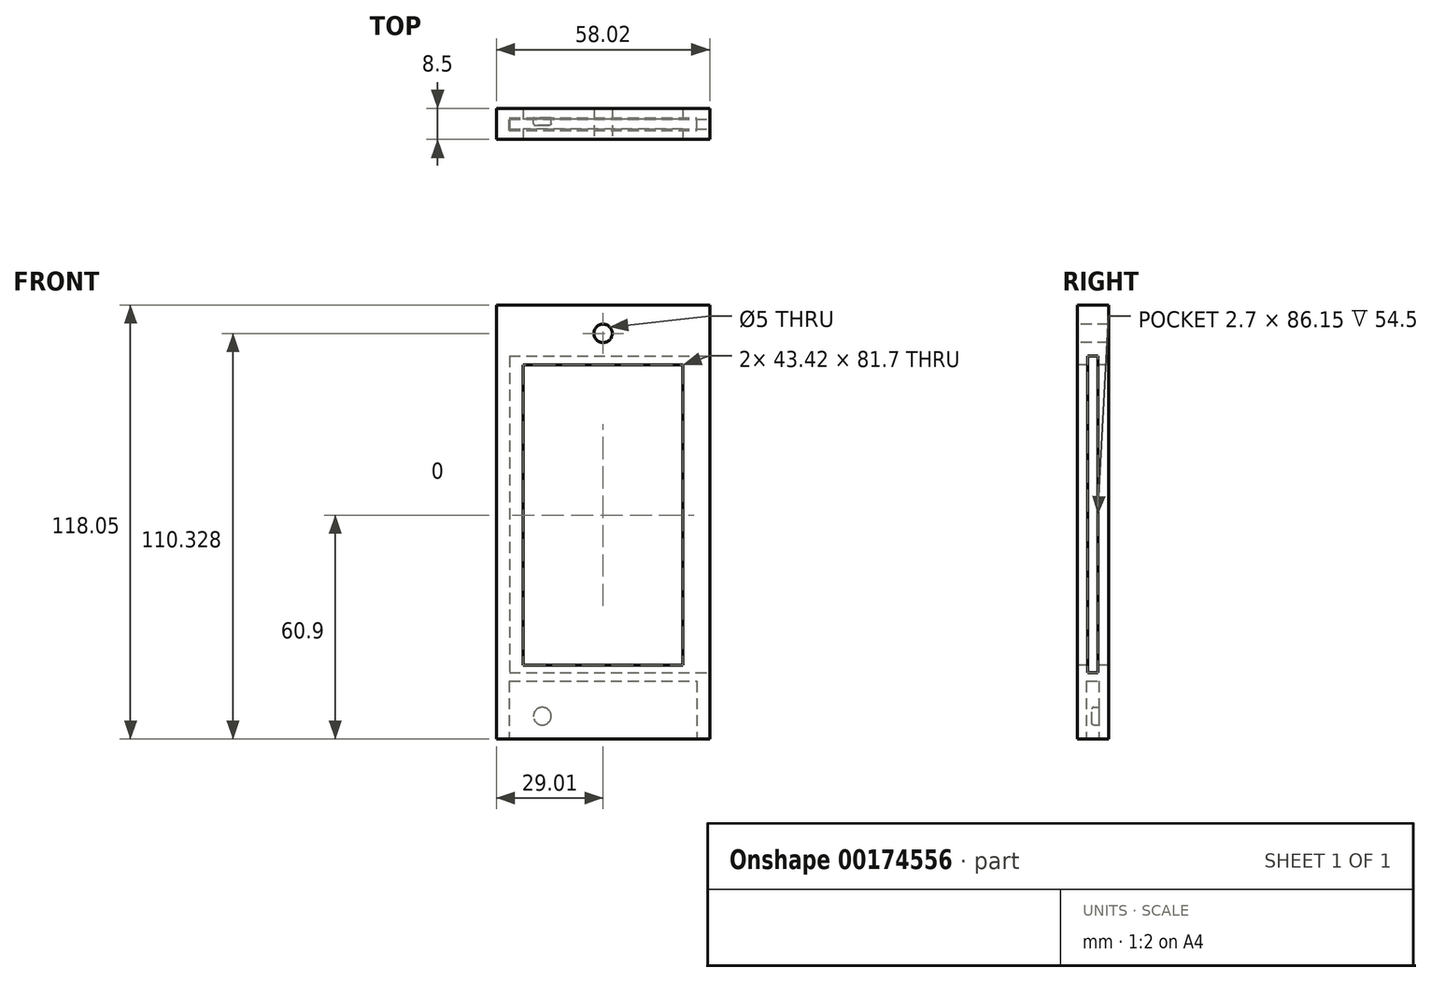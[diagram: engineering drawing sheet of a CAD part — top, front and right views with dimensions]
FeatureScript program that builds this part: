
annotation { "Feature Type Name" : "Feature", "Feature Type Description" : "" }
export const myFeature = defineFeature(function(context is Context, id is Id, definition is map)
    precondition{}
    {
        {
            var Q0;
            Q0=qCreatedBy(makeId("Front.planeOp"),FACE);
            var sketch = newSketch(context, id + "F0", { "sketchPlane" : qUnion([Q0])});
            skLineSegment(sketch, "E0.bottom", {"start": v(-29, 48.15) * mm, "end": v(29.01, 48.15) * mm});
            skLineSegment(sketch, "E0.top", {"start": v(-29.01, -48.15) * mm, "end": v(29.01, -48.15) * mm});
            skLineSegment(sketch, "E0.left", {"start": v(-29, 48.15) * mm, "end": v(-29.01, -48.15) * mm});
            skLineSegment(sketch, "E0.right", {"start": v(29.01, 48.15) * mm, "end": v(29, -48.15) * mm});
            skPoint(sketch, "E0.middle", {"position": v(0, 0) * mm});
            skSolve(sketch);
        }
        {
            var Q0;
            Q0=makeQuery(id+"F0.imprint","IMPRINT",FACE,{"disambiguationData":[TD([[makeQuery(id+"F0.imprint","IMPRINT",EDGE,{"derivedFrom":sQuery(id+"F0.wireOp",EDGE,"E0.bottom")}),-1.0]])]});
            extrude(context, id + "F1", {"entities" : qUnion([Q0]), "depth" : 5.5 * mm});
        }
        {
            var Q0;
            Q0=makeQuery(id+"F1.opExtrude","CAP_FACE",FACE,{"disambiguationData":[OSD([sQuery(id+"F0.wireOp",EDGE,"E0.bottom"),sQuery(id+"F0.wireOp",EDGE,"E0.top"),sQuery(id+"F0.wireOp",EDGE,"E0.left"),sQuery(id+"F0.wireOp",EDGE,"E0.right")])],"isStart":false});
            var sketch = newSketch(context, id + "F2", { "sketchPlane" : qUnion([Q0])});
            skLineSegment(sketch, "E1.bottom", {"start": v(-21.7, 40.85) * mm, "end": v(21.71, 40.85) * mm});
            skLineSegment(sketch, "E1.top", {"start": v(-21.71, -40.85) * mm, "end": v(21.7, -40.85) * mm});
            skLineSegment(sketch, "E1.left", {"start": v(-21.7, 40.85) * mm, "end": v(-21.71, -40.85) * mm});
            skLineSegment(sketch, "E1.right", {"start": v(21.71, 40.85) * mm, "end": v(21.7, -40.85) * mm});
            skPoint(sketch, "E1.middle", {"position": v(0, 0) * mm});
            skSolve(sketch);
        }
        {
            var Q0;
            Q0 = qSketchRegion(id + "F2", true);
            extrude(context, id + "F3", {"entities" : qUnion([Q0]), "operationType" : NewBodyOperationType.REMOVE, "endBound" : BoundingType.THROUGH_ALL, "oppositeDirection" : true, "depth" : 25 * mm});
        }
        {
            var Q0;
            Q0=makeQuery(id+"F1.opExtrude","SWEPT_FACE",FACE,{"disambiguationData":[OSD([sQuery(id+"F0.wireOp",EDGE,"E0.right")])]});
            var sketch = newSketch(context, id + "F4", { "sketchPlane" : qUnion([Q0])});
            skPoint(sketch, "E2", {"position": v(-2.67, 0) * mm});
            skLineSegment(sketch, "E3.bottom", {"start": v(-1.47, 42.88) * mm, "end": v(-3.87, 42.88) * mm});
            skLineSegment(sketch, "E3.top", {"start": v(-1.47, -42.88) * mm, "end": v(-3.87, -42.88) * mm});
            skLineSegment(sketch, "E3.left", {"start": v(-1.47, 42.88) * mm, "end": v(-1.47, -42.88) * mm});
            skLineSegment(sketch, "E3.right", {"start": v(-3.87, 42.88) * mm, "end": v(-3.87, -42.88) * mm});
            skSolve(sketch);
        }
        {
            var Q0;
            Q0 = qSketchRegion(id + "F4", true);
            extrude(context, id + "F5", {"entities" : qUnion([Q0]), "operationType" : NewBodyOperationType.REMOVE, "oppositeDirection" : true, "depth" : 54.5 * mm});
        }
        {
            var Q0;
            Q0=makeQuery(id+"F1.opExtrude","SWEPT_FACE",FACE,{"disambiguationData":[OSD([sQuery(id+"F0.wireOp",EDGE,"E0.bottom")])]});
            extrude(context, id + "F6", {"entities" : qUnion([Q0]), "operationType" : NewBodyOperationType.ADD, "depth" : 9 * mm});
        }
        {
            var Q0;
            {var subQ0=sQuery(id+"F0.wireOp",EDGE,"E0.bottom");Q0=makeQuery(id+"F6.boolean.opBoolean","MERGE",FACE,{"derivedFrom":[makeQuery(id+"F1.opExtrude","CAP_FACE",FACE,{"disambiguationData":[OSD([subQ0,sQuery(id+"F0.wireOp",EDGE,"E0.top"),sQuery(id+"F0.wireOp",EDGE,"E0.left"),sQuery(id+"F0.wireOp",EDGE,"E0.right")])],"isStart":false}),makeQuery(id+"F6.opExtrude","SWEPT_FACE",FACE,{"disambiguationData":[OSD([subQ0]),TDD([makeQuery(id+"F1.opExtrude","CAP_EDGE",EDGE,{"disambiguationData":[OSD([subQ0])],"isStart":false})])]})]});}
            var sketch = newSketch(context, id + "F7", { "sketchPlane" : qUnion([Q0])});
            skPoint(sketch, "E4", {"position": v(0, 49.43) * mm});
            skPoint(sketch, "E4.positionSnap0", {"position": v(0, 57.15) * mm});
            skCircle(sketch, "E5", {"center": v(0, 49.43) * mm, "radius": 2.5 * mm});
            skSolve(sketch);
        }
        {
            var Q0;
            Q0 = qSketchRegion(id + "F7", true);
            extrude(context, id + "F8", {"entities" : qUnion([Q0]), "operationType" : NewBodyOperationType.REMOVE, "endBound" : BoundingType.THROUGH_ALL, "oppositeDirection" : true, "depth" : 25 * mm});
        }
        {
            var Q0;
            Q0=makeQuery(id+"F1.opExtrude","SWEPT_FACE",FACE,{"disambiguationData":[OSD([sQuery(id+"F0.wireOp",EDGE,"E0.top")])]});
            extrude(context, id + "F9", {"entities" : qUnion([Q0]), "operationType" : NewBodyOperationType.ADD, "depth" : 16 * mm});
        }
        {
            var Q0;
            Q0=makeQuery(id+"F9.opExtrude","CAP_FACE",FACE,{"disambiguationData":[OSD([sQuery(id+"F0.wireOp",EDGE,"E0.top")])],"isStart":false});
            var sketch = newSketch(context, id + "F10", { "sketchPlane" : qUnion([Q0])});
            skPoint(sketch, "E6", {"position": v(0, 5.5) * mm});
            skPoint(sketch, "E7", {"position": v(0, 0) * mm});
            skPoint(sketch, "E8", {"position": v(0, 2.75) * mm});
            skLineSegment(sketch, "E9.bottom", {"start": v(-23.5, 4.38) * mm, "end": v(23.5, 4.38) * mm});
            skLineSegment(sketch, "E9.top", {"start": v(-23.5, 1.13) * mm, "end": v(23.5, 1.13) * mm});
            skLineSegment(sketch, "E9.left", {"start": v(-23.5, 4.38) * mm, "end": v(-23.5, 1.12) * mm});
            skLineSegment(sketch, "E9.right", {"start": v(23.5, 4.38) * mm, "end": v(23.5, 1.12) * mm});
            skSolve(sketch);
        }
        {
            var Q0;
            Q0 = qSketchRegion(id + "F10", true);
            extrude(context, id + "F11", {"entities" : qUnion([Q0]), "operationType" : NewBodyOperationType.REMOVE, "oppositeDirection" : true, "depth" : 19 * mm});
        }
        {
            var Q0;
            Q0=makeQuery(id+"F11.boolean.opBoolean","COPY",FACE,{"derivedFrom":makeQuery(id+"F11.opExtrude","SWEPT_FACE",FACE,{"disambiguationData":[OSD([sQuery(id+"F10.wireOp",EDGE,"E9.top")])]})});
            var sketch = newSketch(context, id + "F12", { "sketchPlane" : qUnion([Q0])});
            skPoint(sketch, "E10", {"position": v(-13.86, -45.15) * mm});
            skPoint(sketch, "E11", {"position": v(-13.2, -64.15) * mm});
            skPoint(sketch, "E12", {"position": v(-23.5, -54.65) * mm});
            skPoint(sketch, "E13", {"position": v(28.46, -54.65) * mm});
            skPoint(sketch, "E14", {"position": v(-16.54, -54.65) * mm});
            skCircle(sketch, "E15", {"center": v(-16.54, -54.65) * mm, "radius": 2.4 * mm});
            skSolve(sketch);
        }
        {
            var Q0;
            Q0=makeQuery(id+"F5.boolean.opBoolean","COPY",FACE,{"derivedFrom":makeQuery(id+"F5.opExtrude","SWEPT_FACE",FACE,{"disambiguationData":[OSD([sQuery(id+"F4.wireOp",EDGE,"E3.bottom")])]})});
            extrude(context, id + "F13", {"entities" : qUnion([Q0]), "operationType" : NewBodyOperationType.REMOVE, "oppositeDirection" : true, "depth" : .40 * mm});
        }
        {
            var Q0;
            Q0=makeQuery(id+"F9.opExtrude","CAP_FACE",FACE,{"disambiguationData":[OSD([sQuery(id+"F0.wireOp",EDGE,"E0.top")])],"isStart":false});
            extrude(context, id + "F14", {"entities" : qUnion([Q0]), "operationType" : NewBodyOperationType.REMOVE, "oppositeDirection" : true, "depth" : 3.25 * mm});
        }
        {
            var Q0;
            Q0=makeQuery(id+"F11.boolean.opBoolean","COPY",FACE,{"derivedFrom":makeQuery(id+"F11.opExtrude","SWEPT_FACE",FACE,{"disambiguationData":[OSD([sQuery(id+"F10.wireOp",EDGE,"E9.right")])]})});
            extrude(context, id + "F15", {"entities" : qUnion([Q0]), "operationType" : NewBodyOperationType.REMOVE, "oppositeDirection" : true, "depth" : 2 * mm});
        }
        {
            var Q0;
            Q0=makeQuery(id+"F11.boolean.opBoolean","COPY",FACE,{"derivedFrom":makeQuery(id+"F11.opExtrude","SWEPT_FACE",FACE,{"disambiguationData":[OSD([sQuery(id+"F10.wireOp",EDGE,"E9.left")])]})});
            extrude(context, id + "F16", {"entities" : qUnion([Q0]), "operationType" : NewBodyOperationType.REMOVE, "oppositeDirection" : true, "depth" : 2 * mm});
        }
        {
            var Q0;
            Q0=makeQuery(id+"F12.imprint","IMPRINT",FACE,{"disambiguationData":[TD([[makeQuery(id+"F12.imprint","IMPRINT",EDGE,{"derivedFrom":sQuery(id+"F12.wireOp",EDGE,"E15")}),1.0]])]});
            extrude(context, id + "F17", {"entities" : qUnion([Q0]), "operationType" : NewBodyOperationType.ADD, "depth" : 2 * mm});
        }
        {
            var Q0;
            Q0=makeQuery(id+"F17.opExtrude","CAP_EDGE",EDGE,{"disambiguationData":[OSD([sQuery(id+"F12.wireOp",EDGE,"E15")])],"isStart":false});
            fillet(context, id + "F18", {"entities" : qUnion([Q0]), "radius" : .5 * mm, "tangentPropagation" : true, "allowEdgeOverflow" : false});
        }
        {
            var Q0;
            {var subQ0=sQuery(id+"F4.wireOp",EDGE,"E3.right");Q0=makeQuery(id+"F13.boolean.opBoolean","MERGE",FACE,{"derivedFrom":[makeQuery(id+"F5.boolean.opBoolean","COPY",FACE,{"derivedFrom":makeQuery(id+"F5.opExtrude","SWEPT_FACE",FACE,{"disambiguationData":[OSD([subQ0])]})}),makeQuery(id+"F13.opExtrude","SWEPT_FACE",FACE,{"disambiguationData":[OSD([sQuery(id+"F4.wireOp",EDGE,"E3.bottom"),subQ0])]})]});}
            extrude(context, id + "F19", {"entities" : qUnion([Q0]), "operationType" : NewBodyOperationType.REMOVE, "oppositeDirection" : true, "depth" : .30 * mm});
        }
        {
            var Q0;
            {var subQ0=sQuery(id+"F0.wireOp",EDGE,"E0.top");var subQ1=sQuery(id+"F0.wireOp",EDGE,"E0.bottom");Q0=makeQuery(id+"F9.boolean.opBoolean","MERGE",FACE,{"derivedFrom":[makeQuery(id+"F6.boolean.opBoolean","MERGE",FACE,{"derivedFrom":[makeQuery(id+"F1.opExtrude","CAP_FACE",FACE,{"disambiguationData":[OSD([subQ1,subQ0,sQuery(id+"F0.wireOp",EDGE,"E0.left"),sQuery(id+"F0.wireOp",EDGE,"E0.right")])],"isStart":true}),makeQuery(id+"F6.opExtrude","SWEPT_FACE",FACE,{"disambiguationData":[OSD([subQ1]),TDD([makeQuery(id+"F1.opExtrude","CAP_EDGE",EDGE,{"disambiguationData":[OSD([subQ1])],"isStart":true})])]})]}),makeQuery(id+"F9.opExtrude","SWEPT_FACE",FACE,{"disambiguationData":[OSD([subQ0]),TDD([makeQuery(id+"F1.opExtrude","CAP_EDGE",EDGE,{"disambiguationData":[OSD([subQ0])],"isStart":true})])]})]});}
            extrude(context, id + "F20", {"entities" : qUnion([Q0]), "operationType" : NewBodyOperationType.ADD, "depth" : 1.5 * mm});
        }
        {
            var Q0;
            {var subQ0=sQuery(id+"F0.wireOp",EDGE,"E0.right");var subQ1=sQuery(id+"F0.wireOp",EDGE,"E0.bottom");var subQ2=sQuery(id+"F0.wireOp",EDGE,"E0.left");var subQ3=sQuery(id+"F0.wireOp",EDGE,"E0.top");Q0=makeQuery(id+"FvsBedqHBGxWvc7_1.boolean.opBoolean","SPLIT",FACE,{"disambiguationData":[TD([makeQuery(id+"F1.opExtrude","SWEPT_FACE",FACE,{"disambiguationData":[OSD([subQ2])]})])],"derivedFrom":makeQuery(id+"F9.boolean.opBoolean","MERGE",FACE,{"derivedFrom":[makeQuery(id+"F6.boolean.opBoolean","MERGE",FACE,{"derivedFrom":[makeQuery(id+"F1.opExtrude","CAP_FACE",FACE,{"disambiguationData":[OSD([subQ1,subQ3,subQ2,subQ0])],"isStart":false}),makeQuery(id+"F6.opExtrude","SWEPT_FACE",FACE,{"disambiguationData":[OSD([subQ1]),TDD([makeQuery(id+"F1.opExtrude","CAP_EDGE",EDGE,{"disambiguationData":[OSD([subQ1])],"isStart":false})])]})]}),makeQuery(id+"F9.opExtrude","SWEPT_FACE",FACE,{"disambiguationData":[OSD([subQ3]),TDD([makeQuery(id+"F1.opExtrude","CAP_EDGE",EDGE,{"disambiguationData":[OSD([subQ3])],"isStart":false})])]})]})});}
            extrude(context, id + "F21", {"entities" : qUnion([Q0]), "operationType" : NewBodyOperationType.ADD, "depth" : 1.5 * mm});
        }
        {
            var Q0;
            {var subQ0=sQuery(id+"F10.wireOp",EDGE,"E9.bottom");Q0=makeQuery(id+"F16.boolean.opBoolean","MERGE",FACE,{"derivedFrom":[makeQuery(id+"F15.boolean.opBoolean","MERGE",FACE,{"derivedFrom":[makeQuery(id+"F11.boolean.opBoolean","COPY",FACE,{"derivedFrom":makeQuery(id+"F11.opExtrude","SWEPT_FACE",FACE,{"disambiguationData":[OSD([subQ0])]})}),makeQuery(id+"F15.opExtrude","SWEPT_FACE",FACE,{"disambiguationData":[OSD([subQ0,sQuery(id+"F10.wireOp",EDGE,"E9.right")])]})]}),makeQuery(id+"F16.opExtrude","SWEPT_FACE",FACE,{"disambiguationData":[OSD([subQ0,sQuery(id+"F10.wireOp",EDGE,"E9.left")])]})]});}
            extrude(context, id + "F22", {"entities" : qUnion([Q0]), "operationType" : NewBodyOperationType.REMOVE, "oppositeDirection" : true, "depth" : .2 * mm});
        }
    });
